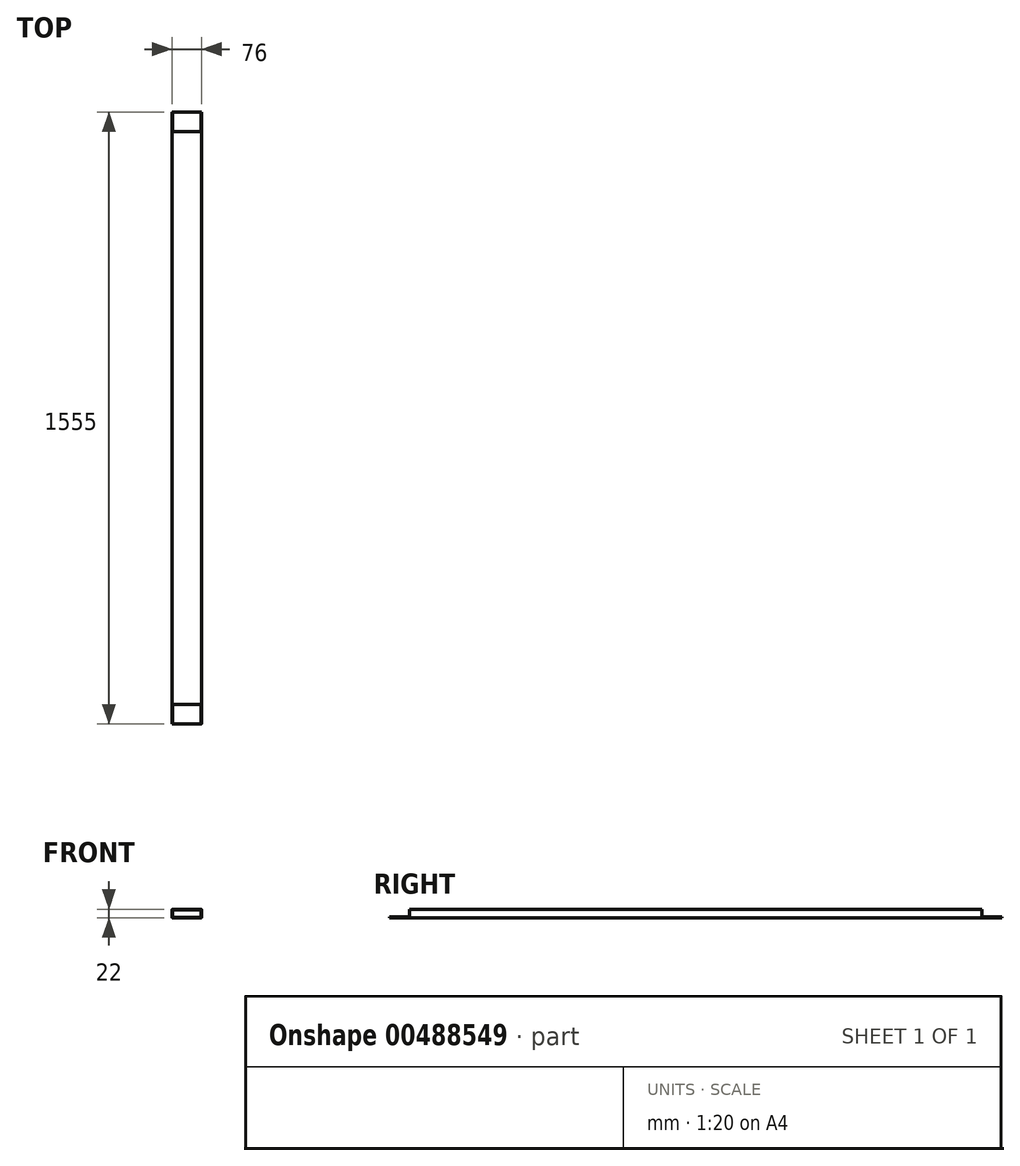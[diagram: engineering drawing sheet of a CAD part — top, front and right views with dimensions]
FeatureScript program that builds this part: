
annotation { "Feature Type Name" : "Feature", "Feature Type Description" : "" }
export const myFeature = defineFeature(function(context is Context, id is Id, definition is map)
    precondition{}
    {
        {
            var Q0;
            Q0=qCreatedBy(makeId("Right.planeOp"),FACE);
            var sketch = newSketch(context, id + "F0", { "sketchPlane" : qUnion([Q0])});
            skLineSegment(sketch, "E0.bottom", {"start": v(777.5, -11) * mm, "end": v(-777.5, -11) * mm});
            skLineSegment(sketch, "E0.top", {"start": v(727.5, 11) * mm, "end": v(-727.5, 11) * mm});
            skLineSegment(sketch, "E0.left", {"start": v(777.5, -11) * mm, "end": v(777.5, -8) * mm});
            skLineSegment(sketch, "E0.right", {"start": v(-777.5, -11) * mm, "end": v(-777.5, -8) * mm});
            skPoint(sketch, "E0.middle", {"position": v(0, 0) * mm});
            skLineSegment(sketch, "E1", {"start": v(-777.5, -8) * mm, "end": v(-727.5, -8) * mm});
            skLineSegment(sketch, "E2", {"start": v(-727.5, -8) * mm, "end": v(-727.5, 11) * mm});
            skLineSegment(sketch, "E3", {"start": v(777.5, -8) * mm, "end": v(727.5, -8) * mm});
            skLineSegment(sketch, "E4", {"start": v(727.5, -8) * mm, "end": v(727.5, 11) * mm});
            skPoint(sketch, "E5.orphan", {"position": v(-777.5, 11) * mm});
            skPoint(sketch, "E6.orphan", {"position": v(777.5, 11) * mm});
            skSolve(sketch);
        }
        {
            var Q0;
            Q0=makeQuery(id+"F0.imprint","IMPRINT",FACE,{"disambiguationData":[TD([[makeQuery(id+"F0.imprint","IMPRINT",EDGE,{"derivedFrom":sQuery(id+"F0.wireOp",EDGE,"E0.bottom")}),-1.0]])]});
            extrude(context, id + "F1", {"entities" : qUnion([Q0]), "depth" : 38 * mm, "hasSecondDirection" : true, "secondDirectionOppositeDirection" : true, "secondDirectionDepth" : 38 * mm});
        }
        {
            var Q0;
            Q0=makeQuery(id+"F1.opExtrude","SWEPT_FACE",FACE,{"disambiguationData":[OSD([sQuery(id+"F0.wireOp",EDGE,"E0.right")])]});
            var sketch = newSketch(context, id + "F2", { "sketchPlane" : qUnion([Q0])});
            skLineSegment(sketch, "E7.bottom", {"start": v(34.5, -9.5) * mm, "end": v(-34.5, -9.5) * mm});
            skLineSegment(sketch, "E7.top", {"start": v(34.5, 9.5) * mm, "end": v(-34.5, 9.5) * mm});
            skLineSegment(sketch, "E7.left", {"start": v(36.5, -7.5) * mm, "end": v(36.5, 7.5) * mm});
            skLineSegment(sketch, "E7.right", {"start": v(-36.5, -7.5) * mm, "end": v(-36.5, 7.5) * mm});
            skPoint(sketch, "E7.middle", {"position": v(0, 0) * mm});
            skPoint(sketch, "E8.visualSharp", {"position": v(-36.5, 9.5) * mm});
            skArc(sketch, "E8.filletArc", {"start": v(-34.5, 9.5) * mm, "mid": v(-35.91, 8.91) * mm, "end": v(-36.5, 7.5) * mm});
            skPoint(sketch, "E9.visualSharp", {"position": v(-36.5, -9.5) * mm});
            skArc(sketch, "E9.filletArc", {"start": v(-36.5, -7.5) * mm, "mid": v(-35.91, -8.91) * mm, "end": v(-34.5, -9.5) * mm});
            skPoint(sketch, "E10.visualSharp", {"position": v(36.5, -9.5) * mm});
            skArc(sketch, "E10.filletArc", {"start": v(34.5, -9.5) * mm, "mid": v(35.91, -8.91) * mm, "end": v(36.5, -7.5) * mm});
            skPoint(sketch, "E11.visualSharp", {"position": v(36.5, 9.5) * mm});
            skArc(sketch, "E11.filletArc", {"start": v(36.5, 7.5) * mm, "mid": v(35.91, 8.91) * mm, "end": v(34.5, 9.5) * mm});
            skSolve(sketch);
        }
        {
            var Q0;
            Q0=makeQuery(id+"F2.imprint","IMPRINT",FACE,{"disambiguationData":[TD([[makeQuery(id+"F2.imprint","IMPRINT",EDGE,{"derivedFrom":sQuery(id+"F2.wireOp",EDGE,"E7.top")}),1.0]])]});
            var Q1;
            {var subQ0=sQuery(id+"F2.wireOp",EDGE,"E7.bottom");Q1=makeQuery(id+"F2.imprint","IMPRINT",FACE,{"disambiguationData":[TD([[makeQuery(id+"F2.imprint","IMPRINT",EDGE,{"derivedFrom":subQ0}),-1.0]])]});}
            extrude(context, id + "F3", {"entities" : qUnion([Q0, Q1]), "operationType" : NewBodyOperationType.REMOVE, "endBound" : BoundingType.THROUGH_ALL, "oppositeDirection" : true, "depth" : 2000 * mm});
        }
        {
            var Q0;
            Q0=makeQuery(id+"F1.opExtrude","CAP_EDGE",EDGE,{"disambiguationData":[OSD([sQuery(id+"F0.wireOp",EDGE,"E0.top")])],"isStart":true});
            var Q1;
            Q1=makeQuery(id+"F1.opExtrude","CAP_EDGE",EDGE,{"disambiguationData":[OSD([sQuery(id+"F0.wireOp",EDGE,"E0.bottom")])],"isStart":true});
            var Q2;
            Q2=makeQuery(id+"F1.opExtrude","CAP_EDGE",EDGE,{"disambiguationData":[OSD([sQuery(id+"F0.wireOp",EDGE,"E0.bottom")])],"isStart":false});
            var Q3;
            Q3=makeQuery(id+"F1.opExtrude","CAP_EDGE",EDGE,{"disambiguationData":[OSD([sQuery(id+"F0.wireOp",EDGE,"E0.top")])],"isStart":false});
            fillet(context, id + "F4", {"entities" : qUnion([Q0, Q1, Q2, Q3]), "radius" : 2 * mm, "tangentPropagation" : true, "allowEdgeOverflow" : false});
        }
    });
